# Revit family: POR_Brenta_J3772_BIM_FR
name_source: partatom
category: Plumbing Fixtures
revit_build: Autodesk Revit 2017 (Build: 20160225_1515(x64)
units: mm (PartAtom-declared; Revit-internal decimal feet)

## family parameters
Always vertical = No
Cut with Voids When Loaded = No
OmniClass Number = 23.45.05.21.11.11
OmniClass Title = Water Operated Water Closets
Part Type = Normal
Room Calculation Point = No
Round Connector Dimension = Use Diameter
Shared = No
Work Plane-Based = No

## types (1)
- J377201 - BRENTA, Vidoir sur pied
    Accessoires = http://www.porcher.com
    Auteur = Ideal Standard
    BIMobject category = Basins
    BIMobject category code = sanitary-basins
    BIMobject main category = Sanitary
    BIMobject main category code = sanitary
    BOSUseNativeGeometries = 1
    Bim-NomDuProjet = POR_Porcher_Basins_J377201
    Brand url = http://www.porcher.com
    Caractéristiques = Vidoir sur pied
sortie horizontale - Poids : 31 kg
    CodeBarre = 8023246216501
    Conformité = NF
    ConseilsDInstallation = www.idealspec.fr
    Cost = 0 $
    Couleur = Blanc
    CoûtDeRemplacement = 0
    Date of publishing = 2018_05_23
    DateDeCréation = 2018_05_23
    Description = BRENTA - Vidoir sur pied
sortie horizontale
    Dimensions = 460 x 460 x 535mm
    DuréeGarantie = ans
    DétailGarantie = Constructeur
    EAN code = https://8023246216501
    Edition number = 1
    Espace = Interne
    Forme = Complexe
    Hauteur = 460 mm  [stored 1.50919 ft]
    IFC Classification = Sanitary Terminal
    IfcExportAs = IfcSanitaryTerminalType
    IfcExportType = Basins
    InformationsProduit = www.idealspec.fr
    Installation instructions = http://www.idealspec.fr
    Largeur = 460 mm  [stored 1.50919 ft]
    Longueur = 535 mm  [stored 1.75525 ft]
    Manufacturer name = Porcher
    Marque = PORCHER
    Material main = Ceramics
    Matériel = Ceramics
    Model = J377201
    NBS Reference Code = 31-79
    NBS Reference Description = Sinks, Wash Basins And Troughs
    Nom = POR_Porcher_Basins_J377201
    Nominal height = 535
    Nominal width = 460
    OmniClass Code = 23-31 13 00
    OmniClass Description = Sinks
    PerformanceAccessibilité = NF
    PoidsNet = 30.8 Kg
    Product Guid = 341b2a8f-1f52-4080-a2af-d0e14f7b058b
    Product SKU = J3772
    Product certification = http://www.idealspec.fr
    Product data url = https://bimobject.com
    Product family = BRENTA
    Product group = Basins
    Product name = BRENTA - Vidoir sur pied
sortie horizontale
    Product url = http://www.idealspec.fr
    Profondeur = 0 mm  [stored 0 ft]
    QR code = http://bimobject.com
    Raccordement = Plomberie
    Référence = J377201
    Révision = 1
    Technical description = http://www.idealspec.fr
    TypeDImmobilisation = Fixe
    URL = http://www.porcher.com
    Uniclass 1.4 Code = L7212
    Uniclass 1.4 Description = Washbasins
    Uniclass 2015 Code = Pr_40_20_96
    Uniclass 2015 Name = Wash basins, sinks and troughs
    Uniclass2015Code = Pr_40_20_96
    Uniclass2015Title = Wash basins, sinks and troughs
    Uniclass2015Version = Products v1.1
    UnitéDeTemps = an
    UrlDuFabricant = http://www.porcher.com
    Version = 1
    Weight Net (Kg) = 30.8

note: [stored X ft] marks values corroborated as IEEE doubles in the binary element streams (Revit-internal decimal feet)

## geometry (parser evidence)
native form markers: Sweep x3
no freeform markers — native parametric forms only
